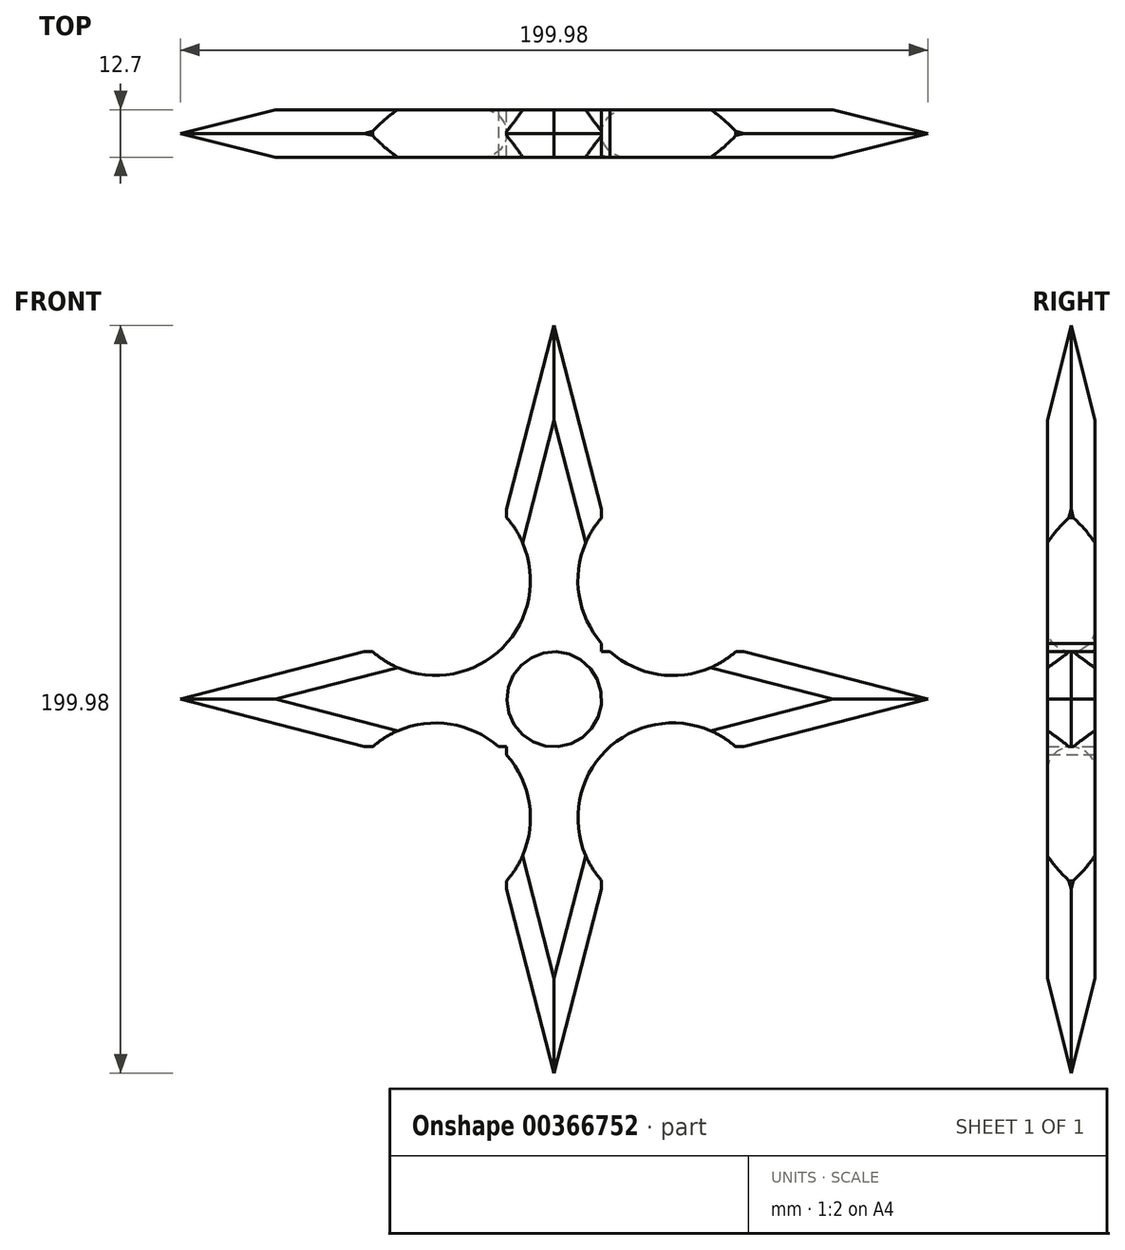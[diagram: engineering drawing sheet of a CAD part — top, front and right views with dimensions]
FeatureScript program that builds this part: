
annotation { "Feature Type Name" : "Feature", "Feature Type Description" : "" }
export const myFeature = defineFeature(function(context is Context, id is Id, definition is map)
    precondition{}
    {
        {
            var Q0;
            Q0=qCreatedBy(makeId("Front.planeOp"),FACE);
            var sketch = newSketch(context, id + "F0", { "sketchPlane" : qUnion([Q0])});
            skCircle(sketch, "E0", {"center": v(0, 0) * mm, "radius": 12.7 * mm});
            skCircle(sketch, "E1", {"center": v(0, 0) * mm, "radius": 19.05 * mm});
            skLineSegment(sketch, "E2.bottom", {"start": v(12.7, -50.8) * mm, "end": v(-12.7, -50.8) * mm});
            skLineSegment(sketch, "E2.top", {"start": v(12.7, 50.8) * mm, "end": v(-12.7, 50.8) * mm});
            skLineSegment(sketch, "E2.left", {"start": v(12.7, -50.8) * mm, "end": v(12.7, 50.8) * mm});
            skLineSegment(sketch, "E2.right", {"start": v(-12.7, -50.8) * mm, "end": v(-12.7, 50.8) * mm});
            skLineSegment(sketch, "E3.bottom", {"start": v(50.8, -12.7) * mm, "end": v(-50.8, -12.7) * mm});
            skLineSegment(sketch, "E3.top", {"start": v(50.8, 12.7) * mm, "end": v(-50.8, 12.7) * mm});
            skLineSegment(sketch, "E3.left", {"start": v(50.8, -12.7) * mm, "end": v(50.8, 12.7) * mm});
            skLineSegment(sketch, "E3.right", {"start": v(-50.8, -12.7) * mm, "end": v(-50.8, 12.7) * mm});
            skLineSegment(sketch, "E4.bottom", {"start": v(31.75, -31.75) * mm, "end": v(-31.75, -31.75) * mm});
            skLineSegment(sketch, "E4.top", {"start": v(31.75, 31.75) * mm, "end": v(-31.75, 31.75) * mm});
            skLineSegment(sketch, "E4.left", {"start": v(31.75, -31.75) * mm, "end": v(31.75, 31.75) * mm});
            skLineSegment(sketch, "E4.right", {"start": v(-31.75, -31.75) * mm, "end": v(-31.75, 31.75) * mm});
            skLineSegment(sketch, "E5", {"start": v(-50.8, -12.7) * mm, "end": v(-99.99, 0) * mm});
            skLineSegment(sketch, "E6", {"start": v(-99.99, 0) * mm, "end": v(-50.8, 12.7) * mm});
            skLineSegment(sketch, "E7", {"start": v(-12.7, -50.8) * mm, "end": v(0, -99.99) * mm});
            skLineSegment(sketch, "E8", {"start": v(0, -99.99) * mm, "end": v(12.7, -50.8) * mm});
            skLineSegment(sketch, "E9", {"start": v(50.8, -12.7) * mm, "end": v(99.99, 0) * mm});
            skLineSegment(sketch, "E10", {"start": v(99.99, 0) * mm, "end": v(50.8, 12.7) * mm});
            skLineSegment(sketch, "E11", {"start": v(12.7, 50.8) * mm, "end": v(0, 99.99) * mm});
            skPoint(sketch, "E11.endSnap0", {"position": v(0, 50.8) * mm});
            skLineSegment(sketch, "E12", {"start": v(0, 99.99) * mm, "end": v(-12.7, 50.8) * mm});
            skSolve(sketch);
        }
        {
            var Q0;
            {var subQ2=sQuery(id+"F0.wireOp",EDGE,"E2.left");var subQ4=sQuery(id+"F0.wireOp",EDGE,"E1");var subQ5=makeQuery(id+"F0.imprint","INTERSECT",VERTEX,{"disambiguationData":[OD(0.0)],"derivedFrom":[subQ4,subQ2]});Q0=makeQuery(id+"F0.imprint","IMPRINT",FACE,{"disambiguationData":[TD([[makeQuery(id+"F0.imprint","IMPRINT",EDGE,{"disambiguationData":[TD([[subQ5,-1.0]])],"derivedFrom":subQ4}),1.0]])]});}
            var Q1;
            {var subQ2=sQuery(id+"F0.wireOp",EDGE,"E3.top");var subQ5=sQuery(id+"F0.wireOp",EDGE,"E1");var subQ8=makeQuery(id+"F0.imprint","INTERSECT",VERTEX,{"disambiguationData":[OD(1.0)],"derivedFrom":[subQ5,subQ2]});Q1=makeQuery(id+"F0.imprint","IMPRINT",FACE,{"disambiguationData":[TD([[makeQuery(id+"F0.imprint","IMPRINT",EDGE,{"disambiguationData":[TD([[subQ8,-1.0]])],"derivedFrom":subQ5}),1.0]])]});}
            var Q2;
            {var subQ4=sQuery(id+"F0.wireOp",EDGE,"E1");var subQ6=sQuery(id+"F0.wireOp",EDGE,"E2.right");var subQ7=makeQuery(id+"F0.imprint","INTERSECT",VERTEX,{"disambiguationData":[OD(1.0)],"derivedFrom":[subQ4,subQ6]});Q2=makeQuery(id+"F0.imprint","IMPRINT",FACE,{"disambiguationData":[TD([[makeQuery(id+"F0.imprint","IMPRINT",EDGE,{"disambiguationData":[TD([[subQ7,-1.0]])],"derivedFrom":subQ4}),1.0]])]});}
            var Q3;
            {var subQ2=sQuery(id+"F0.wireOp",EDGE,"E3.top");var subQ4=sQuery(id+"F0.wireOp",EDGE,"E1");var subQ5=makeQuery(id+"F0.imprint","INTERSECT",VERTEX,{"disambiguationData":[OD(0.0)],"derivedFrom":[subQ4,subQ2]});Q3=makeQuery(id+"F0.imprint","IMPRINT",FACE,{"disambiguationData":[TD([[makeQuery(id+"F0.imprint","IMPRINT",EDGE,{"disambiguationData":[TD([[subQ5,1.0]])],"derivedFrom":subQ4}),1.0]])]});}
            var Q4;
            {var subQ0=sQuery(id+"F0.wireOp",EDGE,"E2.left");var subQ1=sQuery(id+"F0.wireOp",EDGE,"E0");var subQ2=makeQuery(id+"F0.imprint","INTERSECT",VERTEX,{"derivedFrom":[subQ1,subQ0]});Q4=makeQuery(id+"F0.imprint","IMPRINT",FACE,{"disambiguationData":[TD([[makeQuery(id+"F0.imprint","IMPRINT",EDGE,{"disambiguationData":[TD([[subQ2,1.0]])],"derivedFrom":subQ1}),-1.0]])]});}
            var Q5;
            {var subQ0=sQuery(id+"F0.wireOp",EDGE,"E2.right");var subQ1=sQuery(id+"F0.wireOp",EDGE,"E0");var subQ2=makeQuery(id+"F0.imprint","INTERSECT",VERTEX,{"derivedFrom":[subQ1,subQ0]});Q5=makeQuery(id+"F0.imprint","IMPRINT",FACE,{"disambiguationData":[TD([[makeQuery(id+"F0.imprint","IMPRINT",EDGE,{"disambiguationData":[TD([[subQ2,-1.0]])],"derivedFrom":subQ1}),-1.0]])]});}
            var Q6;
            {var subQ0=sQuery(id+"F0.wireOp",EDGE,"E3.top");var subQ1=sQuery(id+"F0.wireOp",EDGE,"E0");var subQ2=makeQuery(id+"F0.imprint","INTERSECT",VERTEX,{"derivedFrom":[subQ1,subQ0]});Q6=makeQuery(id+"F0.imprint","IMPRINT",FACE,{"disambiguationData":[TD([[makeQuery(id+"F0.imprint","IMPRINT",EDGE,{"disambiguationData":[TD([[subQ2,-1.0]])],"derivedFrom":subQ1}),-1.0]])]});}
            var Q7;
            {var subQ0=sQuery(id+"F0.wireOp",EDGE,"E3.top");var subQ1=sQuery(id+"F0.wireOp",EDGE,"E0");var subQ2=makeQuery(id+"F0.imprint","INTERSECT",VERTEX,{"derivedFrom":[subQ1,subQ0]});Q7=makeQuery(id+"F0.imprint","IMPRINT",FACE,{"disambiguationData":[TD([[makeQuery(id+"F0.imprint","IMPRINT",EDGE,{"disambiguationData":[TD([[subQ2,1.0]])],"derivedFrom":subQ1}),-1.0]])]});}
            var Q8;
            {var subQ3=sQuery(id+"F0.wireOp",EDGE,"E2.left");var subQ5=sQuery(id+"F0.wireOp",EDGE,"E1");var subQ6=makeQuery(id+"F0.imprint","INTERSECT",VERTEX,{"disambiguationData":[OD(0.0)],"derivedFrom":[subQ5,subQ3]});Q8=makeQuery(id+"F0.imprint","IMPRINT",FACE,{"disambiguationData":[TD([[makeQuery(id+"F0.imprint","IMPRINT",EDGE,{"disambiguationData":[TD([[subQ6,1.0]])],"derivedFrom":subQ5}),-1.0]])]});}
            var Q9;
            {var subQ0=sQuery(id+"F0.wireOp",EDGE,"E2.left");var subQ1=sQuery(id+"F0.wireOp",EDGE,"E1");var subQ2=makeQuery(id+"F0.imprint","INTERSECT",VERTEX,{"disambiguationData":[OD(0.0)],"derivedFrom":[subQ1,subQ0]});Q9=makeQuery(id+"F0.imprint","IMPRINT",FACE,{"disambiguationData":[TD([[makeQuery(id+"F0.imprint","IMPRINT",EDGE,{"disambiguationData":[TD([[subQ2,-1.0]])],"derivedFrom":subQ1}),-1.0]])]});}
            var Q10;
            {var subQ3=sQuery(id+"F0.wireOp",EDGE,"E1");var subQ7=sQuery(id+"F0.wireOp",EDGE,"E2.right");var subQ9=makeQuery(id+"F0.imprint","INTERSECT",VERTEX,{"disambiguationData":[OD(0.0)],"derivedFrom":[subQ3,subQ7]});Q10=makeQuery(id+"F0.imprint","IMPRINT",FACE,{"disambiguationData":[TD([[makeQuery(id+"F0.imprint","IMPRINT",EDGE,{"disambiguationData":[TD([[subQ9,-1.0]])],"derivedFrom":subQ3}),-1.0]])]});}
            var Q11;
            {var subQ0=sQuery(id+"F0.wireOp",EDGE,"E3.top");var subQ1=sQuery(id+"F0.wireOp",EDGE,"E1");var subQ2=makeQuery(id+"F0.imprint","INTERSECT",VERTEX,{"disambiguationData":[OD(1.0)],"derivedFrom":[subQ1,subQ0]});Q11=makeQuery(id+"F0.imprint","IMPRINT",FACE,{"disambiguationData":[TD([[makeQuery(id+"F0.imprint","IMPRINT",EDGE,{"disambiguationData":[TD([[subQ2,-1.0]])],"derivedFrom":subQ1}),-1.0]])]});}
            var Q12;
            {var subQ5=sQuery(id+"F0.wireOp",EDGE,"E3.bottom");var subQ7=sQuery(id+"F0.wireOp",EDGE,"E1");var subQ8=makeQuery(id+"F0.imprint","INTERSECT",VERTEX,{"disambiguationData":[OD(0.0)],"derivedFrom":[subQ7,subQ5]});Q12=makeQuery(id+"F0.imprint","IMPRINT",FACE,{"disambiguationData":[TD([[makeQuery(id+"F0.imprint","IMPRINT",EDGE,{"disambiguationData":[TD([[subQ8,-1.0]])],"derivedFrom":subQ7}),-1.0]])]});}
            var Q13;
            {var subQ0=sQuery(id+"F0.wireOp",EDGE,"E2.right");var subQ1=sQuery(id+"F0.wireOp",EDGE,"E1");var subQ2=makeQuery(id+"F0.imprint","INTERSECT",VERTEX,{"disambiguationData":[OD(1.0)],"derivedFrom":[subQ1,subQ0]});Q13=makeQuery(id+"F0.imprint","IMPRINT",FACE,{"disambiguationData":[TD([[makeQuery(id+"F0.imprint","IMPRINT",EDGE,{"disambiguationData":[TD([[subQ2,-1.0]])],"derivedFrom":subQ1}),-1.0]])]});}
            var Q14;
            {var subQ3=sQuery(id+"F0.wireOp",EDGE,"E2.left");var subQ5=sQuery(id+"F0.wireOp",EDGE,"E1");var subQ6=makeQuery(id+"F0.imprint","INTERSECT",VERTEX,{"disambiguationData":[OD(1.0)],"derivedFrom":[subQ5,subQ3]});Q14=makeQuery(id+"F0.imprint","IMPRINT",FACE,{"disambiguationData":[TD([[makeQuery(id+"F0.imprint","IMPRINT",EDGE,{"disambiguationData":[TD([[subQ6,-1.0]])],"derivedFrom":subQ5}),-1.0]])]});}
            var Q15;
            {var subQ0=sQuery(id+"F0.wireOp",EDGE,"E3.top");var subQ1=sQuery(id+"F0.wireOp",EDGE,"E1");var subQ2=makeQuery(id+"F0.imprint","INTERSECT",VERTEX,{"disambiguationData":[OD(0.0)],"derivedFrom":[subQ1,subQ0]});Q15=makeQuery(id+"F0.imprint","IMPRINT",FACE,{"disambiguationData":[TD([[makeQuery(id+"F0.imprint","IMPRINT",EDGE,{"disambiguationData":[TD([[subQ2,1.0]])],"derivedFrom":subQ1}),-1.0]])]});}
            var Q16;
            {var subQ0=sQuery(id+"F0.wireOp",EDGE,"E3.left");Q16=makeQuery(id+"F0.imprint","IMPRINT",FACE,{"disambiguationData":[TD([[makeQuery(id+"F0.imprint","IMPRINT",EDGE,{"derivedFrom":subQ0}),1.0]])]});}
            var Q17;
            Q17=makeQuery(id+"F0.imprint","IMPRINT",FACE,{"disambiguationData":[TD([[makeQuery(id+"F0.imprint","IMPRINT",EDGE,{"derivedFrom":sQuery(id+"F0.wireOp",EDGE,"E3.left")}),-1.0]])]});
            var Q18;
            Q18=makeQuery(id+"F0.imprint","IMPRINT",FACE,{"disambiguationData":[TD([[makeQuery(id+"F0.imprint","IMPRINT",EDGE,{"derivedFrom":sQuery(id+"F0.wireOp",EDGE,"E2.top")}),-1.0]])]});
            var Q19;
            {var subQ0=sQuery(id+"F0.wireOp",EDGE,"E2.top");Q19=makeQuery(id+"F0.imprint","IMPRINT",FACE,{"disambiguationData":[TD([[makeQuery(id+"F0.imprint","IMPRINT",EDGE,{"derivedFrom":subQ0}),1.0]])]});}
            var Q20;
            {var subQ0=sQuery(id+"F0.wireOp",EDGE,"E3.right");Q20=makeQuery(id+"F0.imprint","IMPRINT",FACE,{"disambiguationData":[TD([[makeQuery(id+"F0.imprint","IMPRINT",EDGE,{"derivedFrom":subQ0}),-1.0]])]});}
            var Q21;
            Q21=makeQuery(id+"F0.imprint","IMPRINT",FACE,{"disambiguationData":[TD([[makeQuery(id+"F0.imprint","IMPRINT",EDGE,{"derivedFrom":sQuery(id+"F0.wireOp",EDGE,"E3.right")}),1.0]])]});
            var Q22;
            Q22=makeQuery(id+"F0.imprint","IMPRINT",FACE,{"disambiguationData":[TD([[makeQuery(id+"F0.imprint","IMPRINT",EDGE,{"derivedFrom":sQuery(id+"F0.wireOp",EDGE,"E2.bottom")}),1.0]])]});
            var Q23;
            {var subQ0=sQuery(id+"F0.wireOp",EDGE,"E2.bottom");Q23=makeQuery(id+"F0.imprint","IMPRINT",FACE,{"disambiguationData":[TD([[makeQuery(id+"F0.imprint","IMPRINT",EDGE,{"derivedFrom":subQ0}),-1.0]])]});}
            var Q24;
            {var subQ0=sQuery(id+"F0.wireOp",EDGE,"E2.left");var subQ1=sQuery(id+"F0.wireOp",EDGE,"E1");var subQ2=makeQuery(id+"F0.imprint","INTERSECT",VERTEX,{"disambiguationData":[OD(1.0)],"derivedFrom":[subQ1,subQ0]});Q24=makeQuery(id+"F0.imprint","IMPRINT",FACE,{"disambiguationData":[TD([[makeQuery(id+"F0.imprint","IMPRINT",EDGE,{"disambiguationData":[TD([[subQ2,-1.0]])],"derivedFrom":subQ1}),1.0]])]});}
            var Q25;
            {var subQ0=sQuery(id+"F0.wireOp",EDGE,"E3.bottom");var subQ1=sQuery(id+"F0.wireOp",EDGE,"E1");var subQ2=makeQuery(id+"F0.imprint","INTERSECT",VERTEX,{"disambiguationData":[OD(0.0)],"derivedFrom":[subQ1,subQ0]});Q25=makeQuery(id+"F0.imprint","IMPRINT",FACE,{"disambiguationData":[TD([[makeQuery(id+"F0.imprint","IMPRINT",EDGE,{"disambiguationData":[TD([[subQ2,-1.0]])],"derivedFrom":subQ1}),1.0]])]});}
            var Q26;
            {var subQ0=sQuery(id+"F0.wireOp",EDGE,"E2.right");var subQ1=sQuery(id+"F0.wireOp",EDGE,"E1");var subQ2=makeQuery(id+"F0.imprint","INTERSECT",VERTEX,{"disambiguationData":[OD(0.0)],"derivedFrom":[subQ1,subQ0]});Q26=makeQuery(id+"F0.imprint","IMPRINT",FACE,{"disambiguationData":[TD([[makeQuery(id+"F0.imprint","IMPRINT",EDGE,{"disambiguationData":[TD([[subQ2,-1.0]])],"derivedFrom":subQ1}),1.0]])]});}
            var Q27;
            {var subQ0=sQuery(id+"F0.wireOp",EDGE,"E2.left");var subQ1=sQuery(id+"F0.wireOp",EDGE,"E1");var subQ2=makeQuery(id+"F0.imprint","INTERSECT",VERTEX,{"disambiguationData":[OD(0.0)],"derivedFrom":[subQ1,subQ0]});Q27=makeQuery(id+"F0.imprint","IMPRINT",FACE,{"disambiguationData":[TD([[makeQuery(id+"F0.imprint","IMPRINT",EDGE,{"disambiguationData":[TD([[subQ2,1.0]])],"derivedFrom":subQ1}),1.0]])]});}
            extrude(context, id + "F1", {"entities" : qUnion([Q0, Q1, Q2, Q3, Q4, Q5, Q6, Q7, Q8, Q9, Q10, Q11, Q12, Q13, Q14, Q15, Q16, Q17, Q18, Q19, Q20, Q21, Q22, Q23, Q24, Q25, Q26, Q27]), "depth" : 12.7 * mm});
        }
        {
            var Q0;
            Q0=makeQuery(id+"F1.opExtrude","CAP_FACE",FACE,{"disambiguationData":[OSD([sQuery(id+"F0.wireOp",EDGE,"E0"),sQuery(id+"F0.wireOp",EDGE,"E1"),sQuery(id+"F0.wireOp",EDGE,"E2.left"),sQuery(id+"F0.wireOp",EDGE,"E2.right"),sQuery(id+"F0.wireOp",EDGE,"E3.bottom"),sQuery(id+"F0.wireOp",EDGE,"E3.top"),sQuery(id+"F0.wireOp",EDGE,"E4.bottom"),sQuery(id+"F0.wireOp",EDGE,"E4.top"),sQuery(id+"F0.wireOp",EDGE,"E4.left"),sQuery(id+"F0.wireOp",EDGE,"E4.right"),sQuery(id+"F0.wireOp",EDGE,"E5"),sQuery(id+"F0.wireOp",EDGE,"E6"),sQuery(id+"F0.wireOp",EDGE,"E7"),sQuery(id+"F0.wireOp",EDGE,"E8"),sQuery(id+"F0.wireOp",EDGE,"E9"),sQuery(id+"F0.wireOp",EDGE,"E10"),sQuery(id+"F0.wireOp",EDGE,"E11"),sQuery(id+"F0.wireOp",EDGE,"E12")])],"isStart":false});
            var sketch = newSketch(context, id + "F2", { "sketchPlane" : qUnion([Q0])});
            skLineSegment(sketch, "E13", {"start": v(-31.75, 31.75) * mm, "end": v(31.75, 31.75) * mm});
            skLineSegment(sketch, "E14", {"start": v(31.75, 31.75) * mm, "end": v(31.75, -31.75) * mm});
            skLineSegment(sketch, "E15", {"start": v(31.75, -31.75) * mm, "end": v(-31.75, -31.75) * mm});
            skLineSegment(sketch, "E16", {"start": v(-31.75, -31.75) * mm, "end": v(-31.75, 31.75) * mm});
            skSolve(sketch);
        }
        {
            var Q0;
            Q0=sQuery(id+"F2.wireOp",VERTEX,"E13.start");
            var Q1;
            Q1=sQuery(id+"F2.wireOp",VERTEX,"E16.start");
            var Q2;
            Q2=sQuery(id+"F2.wireOp",VERTEX,"E15.start");
            var Q3;
            Q3=sQuery(id+"F2.wireOp",VERTEX,"E14.start");
            var Q4;
            Q4=makeQuery(id+"F1.opExtrude","SWEPT_BODY",BODY,{"disambiguationData":[OSD([sQuery(id+"F0.wireOp",EDGE,"E0"),sQuery(id+"F0.wireOp",EDGE,"E1"),sQuery(id+"F0.wireOp",EDGE,"E2.left"),sQuery(id+"F0.wireOp",EDGE,"E2.right"),sQuery(id+"F0.wireOp",EDGE,"E3.bottom"),sQuery(id+"F0.wireOp",EDGE,"E3.top"),sQuery(id+"F0.wireOp",EDGE,"E4.bottom"),sQuery(id+"F0.wireOp",EDGE,"E4.top"),sQuery(id+"F0.wireOp",EDGE,"E4.left"),sQuery(id+"F0.wireOp",EDGE,"E4.right"),sQuery(id+"F0.wireOp",EDGE,"E5"),sQuery(id+"F0.wireOp",EDGE,"E6"),sQuery(id+"F0.wireOp",EDGE,"E7"),sQuery(id+"F0.wireOp",EDGE,"E8"),sQuery(id+"F0.wireOp",EDGE,"E9"),sQuery(id+"F0.wireOp",EDGE,"E10"),sQuery(id+"F0.wireOp",EDGE,"E11"),sQuery(id+"F0.wireOp",EDGE,"E12")])]});
            hole(context, id + "F3", {"style" : HoleStyle.SIMPLE, "endStyle" : HoleEndStyle.THROUGH, "holeDiameter" : 50.8 * mm, "tappedDepth" : 12.7 * mm, "tapClearance" : 3, "locations" : qUnion([Q0, Q1, Q2, Q3]), "scope" : qUnion([Q4])});
        }
        {
            var Q0;
            Q0=makeQuery(id+"F1.opExtrude","CAP_EDGE",EDGE,{"disambiguationData":[OSD([sQuery(id+"F0.wireOp",EDGE,"E6")])],"isStart":false});
            var Q1;
            Q1=makeQuery(id+"F1.opExtrude","CAP_EDGE",EDGE,{"disambiguationData":[OSD([sQuery(id+"F0.wireOp",EDGE,"E5")])],"isStart":false});
            var Q2;
            Q2=makeQuery(id+"F1.opExtrude","CAP_EDGE",EDGE,{"disambiguationData":[OSD([sQuery(id+"F0.wireOp",EDGE,"E5")])],"isStart":true});
            var Q3;
            Q3=makeQuery(id+"F1.opExtrude","CAP_EDGE",EDGE,{"disambiguationData":[OSD([sQuery(id+"F0.wireOp",EDGE,"E6")])],"isStart":true});
            var Q4;
            Q4=makeQuery(id+"F1.opExtrude","CAP_EDGE",EDGE,{"disambiguationData":[OSD([sQuery(id+"F0.wireOp",EDGE,"E11")])],"isStart":false});
            var Q5;
            Q5=makeQuery(id+"F1.opExtrude","CAP_EDGE",EDGE,{"disambiguationData":[OSD([sQuery(id+"F0.wireOp",EDGE,"E12")])],"isStart":false});
            var Q6;
            Q6=makeQuery(id+"F1.opExtrude","CAP_EDGE",EDGE,{"disambiguationData":[OSD([sQuery(id+"F0.wireOp",EDGE,"E12")])],"isStart":true});
            var Q7;
            Q7=makeQuery(id+"F1.opExtrude","CAP_EDGE",EDGE,{"disambiguationData":[OSD([sQuery(id+"F0.wireOp",EDGE,"E11")])],"isStart":true});
            var Q8;
            Q8=makeQuery(id+"F1.opExtrude","CAP_EDGE",EDGE,{"disambiguationData":[OSD([sQuery(id+"F0.wireOp",EDGE,"E10")])],"isStart":true});
            var Q9;
            Q9=makeQuery(id+"F1.opExtrude","CAP_EDGE",EDGE,{"disambiguationData":[OSD([sQuery(id+"F0.wireOp",EDGE,"E10")])],"isStart":false});
            var Q10;
            Q10=makeQuery(id+"F1.opExtrude","CAP_EDGE",EDGE,{"disambiguationData":[OSD([sQuery(id+"F0.wireOp",EDGE,"E9")])],"isStart":true});
            var Q11;
            Q11=makeQuery(id+"F1.opExtrude","CAP_EDGE",EDGE,{"disambiguationData":[OSD([sQuery(id+"F0.wireOp",EDGE,"E9")])],"isStart":false});
            var Q12;
            Q12=makeQuery(id+"F1.opExtrude","CAP_EDGE",EDGE,{"disambiguationData":[OSD([sQuery(id+"F0.wireOp",EDGE,"E7")])],"isStart":true});
            var Q13;
            Q13=makeQuery(id+"F1.opExtrude","CAP_EDGE",EDGE,{"disambiguationData":[OSD([sQuery(id+"F0.wireOp",EDGE,"E8")])],"isStart":true});
            var Q14;
            Q14=makeQuery(id+"F1.opExtrude","CAP_EDGE",EDGE,{"disambiguationData":[OSD([sQuery(id+"F0.wireOp",EDGE,"E8")])],"isStart":false});
            var Q15;
            Q15=makeQuery(id+"F1.opExtrude","CAP_EDGE",EDGE,{"disambiguationData":[OSD([sQuery(id+"F0.wireOp",EDGE,"E7")])],"isStart":false});
            chamfer(context, id + "F4", {"entities" : qUnion([Q0, Q1, Q2, Q3, Q4, Q5, Q6, Q7, Q8, Q9, Q10, Q11, Q12, Q13, Q14, Q15]), "chamferType" : ChamferType.OFFSET_ANGLE, "width" : 6.35 * mm, "oppositeDirection" : false, "angle" : 45 * degree, "tangentPropagation" : true});
        }
        {
            var Q0;
            Q0=makeQuery(id+"F1.opExtrude","CAP_EDGE",EDGE,{"disambiguationData":[OSD([sQuery(id+"F0.wireOp",EDGE,"E0")])],"isStart":true});
            var Q1;
            Q1=makeQuery(id+"F1.opExtrude","CAP_EDGE",EDGE,{"disambiguationData":[OSD([sQuery(id+"F0.wireOp",EDGE,"E0")])],"isStart":false});
            var Q2;
            Q2=makeQuery(id+"F3.hole-2.boolean.opBoolean","INTERSECT",EDGE,{"derivedFrom":[makeQuery(id+"F1.opExtrude","CAP_FACE",FACE,{"disambiguationData":[OSD([sQuery(id+"F0.wireOp",EDGE,"E0"),sQuery(id+"F0.wireOp",EDGE,"E2.left"),sQuery(id+"F0.wireOp",EDGE,"E2.right"),sQuery(id+"F0.wireOp",EDGE,"E3.bottom"),sQuery(id+"F0.wireOp",EDGE,"E3.top"),sQuery(id+"F0.wireOp",EDGE,"E4.bottom"),sQuery(id+"F0.wireOp",EDGE,"E4.top"),sQuery(id+"F0.wireOp",EDGE,"E4.left"),sQuery(id+"F0.wireOp",EDGE,"E4.right"),sQuery(id+"F0.wireOp",EDGE,"E5"),sQuery(id+"F0.wireOp",EDGE,"E6"),sQuery(id+"F0.wireOp",EDGE,"E7"),sQuery(id+"F0.wireOp",EDGE,"E8"),sQuery(id+"F0.wireOp",EDGE,"E9"),sQuery(id+"F0.wireOp",EDGE,"E10"),sQuery(id+"F0.wireOp",EDGE,"E11"),sQuery(id+"F0.wireOp",EDGE,"E12")])],"isStart":true}),makeQuery(id+"F3.hole-2.opRevolve","SWEPT_FACE",FACE,{"disambiguationData":[OSD([sQuery(id+"F3.hole-2.sketch.wireOp",EDGE,"core_line_2")])]})]});
            var Q3;
            Q3=makeQuery(id+"F3.hole-1.boolean.opBoolean","INTERSECT",EDGE,{"derivedFrom":[makeQuery(id+"F1.opExtrude","CAP_FACE",FACE,{"disambiguationData":[OSD([sQuery(id+"F0.wireOp",EDGE,"E0"),sQuery(id+"F0.wireOp",EDGE,"E2.left"),sQuery(id+"F0.wireOp",EDGE,"E2.right"),sQuery(id+"F0.wireOp",EDGE,"E3.bottom"),sQuery(id+"F0.wireOp",EDGE,"E3.top"),sQuery(id+"F0.wireOp",EDGE,"E4.bottom"),sQuery(id+"F0.wireOp",EDGE,"E4.top"),sQuery(id+"F0.wireOp",EDGE,"E4.left"),sQuery(id+"F0.wireOp",EDGE,"E4.right"),sQuery(id+"F0.wireOp",EDGE,"E5"),sQuery(id+"F0.wireOp",EDGE,"E6"),sQuery(id+"F0.wireOp",EDGE,"E7"),sQuery(id+"F0.wireOp",EDGE,"E8"),sQuery(id+"F0.wireOp",EDGE,"E9"),sQuery(id+"F0.wireOp",EDGE,"E10"),sQuery(id+"F0.wireOp",EDGE,"E11"),sQuery(id+"F0.wireOp",EDGE,"E12")])],"isStart":true}),makeQuery(id+"F3.hole-1.opRevolve","SWEPT_FACE",FACE,{"disambiguationData":[OSD([sQuery(id+"F3.hole-1.sketch.wireOp",EDGE,"core_line_2")])]})]});
            var Q4;
            Q4=makeQuery(id+"F3.hole-3.boolean.opBoolean","INTERSECT",EDGE,{"derivedFrom":[makeQuery(id+"F1.opExtrude","CAP_FACE",FACE,{"disambiguationData":[OSD([sQuery(id+"F0.wireOp",EDGE,"E0"),sQuery(id+"F0.wireOp",EDGE,"E2.left"),sQuery(id+"F0.wireOp",EDGE,"E2.right"),sQuery(id+"F0.wireOp",EDGE,"E3.bottom"),sQuery(id+"F0.wireOp",EDGE,"E3.top"),sQuery(id+"F0.wireOp",EDGE,"E4.bottom"),sQuery(id+"F0.wireOp",EDGE,"E4.top"),sQuery(id+"F0.wireOp",EDGE,"E4.left"),sQuery(id+"F0.wireOp",EDGE,"E4.right"),sQuery(id+"F0.wireOp",EDGE,"E5"),sQuery(id+"F0.wireOp",EDGE,"E6"),sQuery(id+"F0.wireOp",EDGE,"E7"),sQuery(id+"F0.wireOp",EDGE,"E8"),sQuery(id+"F0.wireOp",EDGE,"E9"),sQuery(id+"F0.wireOp",EDGE,"E10"),sQuery(id+"F0.wireOp",EDGE,"E11"),sQuery(id+"F0.wireOp",EDGE,"E12")])],"isStart":true}),makeQuery(id+"F3.hole-3.opRevolve","SWEPT_FACE",FACE,{"disambiguationData":[OSD([sQuery(id+"F3.hole-3.sketch.wireOp",EDGE,"core_line_2")])]})]});
            var Q5;
            Q5=makeQuery(id+"F3.hole-3.boolean.opBoolean","COPY",EDGE,{"derivedFrom":makeQuery(id+"F3.hole-3.opRevolve","SWEPT_EDGE",EDGE,{"disambiguationData":[OSD([sQuery(id+"F3.hole-3.sketch.wireOp",EDGE,"core_line_2"),sQuery(id+"F3.hole-3.sketch.wireOp",EDGE,"core_line_3")])]})});
            var Q6;
            Q6=makeQuery(id+"F3.hole-0.boolean.opBoolean","INTERSECT",EDGE,{"derivedFrom":[makeQuery(id+"F1.opExtrude","CAP_FACE",FACE,{"disambiguationData":[OSD([sQuery(id+"F0.wireOp",EDGE,"E0"),sQuery(id+"F0.wireOp",EDGE,"E2.left"),sQuery(id+"F0.wireOp",EDGE,"E2.right"),sQuery(id+"F0.wireOp",EDGE,"E3.bottom"),sQuery(id+"F0.wireOp",EDGE,"E3.top"),sQuery(id+"F0.wireOp",EDGE,"E4.bottom"),sQuery(id+"F0.wireOp",EDGE,"E4.top"),sQuery(id+"F0.wireOp",EDGE,"E4.left"),sQuery(id+"F0.wireOp",EDGE,"E4.right"),sQuery(id+"F0.wireOp",EDGE,"E5"),sQuery(id+"F0.wireOp",EDGE,"E6"),sQuery(id+"F0.wireOp",EDGE,"E7"),sQuery(id+"F0.wireOp",EDGE,"E8"),sQuery(id+"F0.wireOp",EDGE,"E9"),sQuery(id+"F0.wireOp",EDGE,"E10"),sQuery(id+"F0.wireOp",EDGE,"E11"),sQuery(id+"F0.wireOp",EDGE,"E12")])],"isStart":true}),makeQuery(id+"F3.hole-0.opRevolve","SWEPT_FACE",FACE,{"disambiguationData":[OSD([sQuery(id+"F3.hole-0.sketch.wireOp",EDGE,"core_line_2")])]})]});
            var Q7;
            Q7=makeQuery(id+"F3.hole-0.boolean.opBoolean","COPY",EDGE,{"derivedFrom":makeQuery(id+"F3.hole-0.opRevolve","SWEPT_EDGE",EDGE,{"disambiguationData":[OSD([sQuery(id+"F3.hole-0.sketch.wireOp",EDGE,"core_line_2"),sQuery(id+"F3.hole-0.sketch.wireOp",EDGE,"core_line_3")])]})});
            var Q8;
            Q8=makeQuery(id+"F3.hole-2.boolean.opBoolean","COPY",EDGE,{"derivedFrom":makeQuery(id+"F3.hole-2.opRevolve","SWEPT_EDGE",EDGE,{"disambiguationData":[OSD([sQuery(id+"F3.hole-2.sketch.wireOp",EDGE,"core_line_2"),sQuery(id+"F3.hole-2.sketch.wireOp",EDGE,"core_line_3")])]})});
            var Q9;
            Q9=makeQuery(id+"F3.hole-1.boolean.opBoolean","COPY",EDGE,{"derivedFrom":makeQuery(id+"F3.hole-1.opRevolve","SWEPT_EDGE",EDGE,{"disambiguationData":[OSD([sQuery(id+"F3.hole-1.sketch.wireOp",EDGE,"core_line_2"),sQuery(id+"F3.hole-1.sketch.wireOp",EDGE,"core_line_3")])]})});
            fillet(context, id + "F5", {"entities" : qUnion([Q0, Q1, Q2, Q3, Q4, Q5, Q6, Q7, Q8, Q9]), "radius" : 6.35 * mm, "tangentPropagation" : true, "allowEdgeOverflow" : false});
        }
    });
